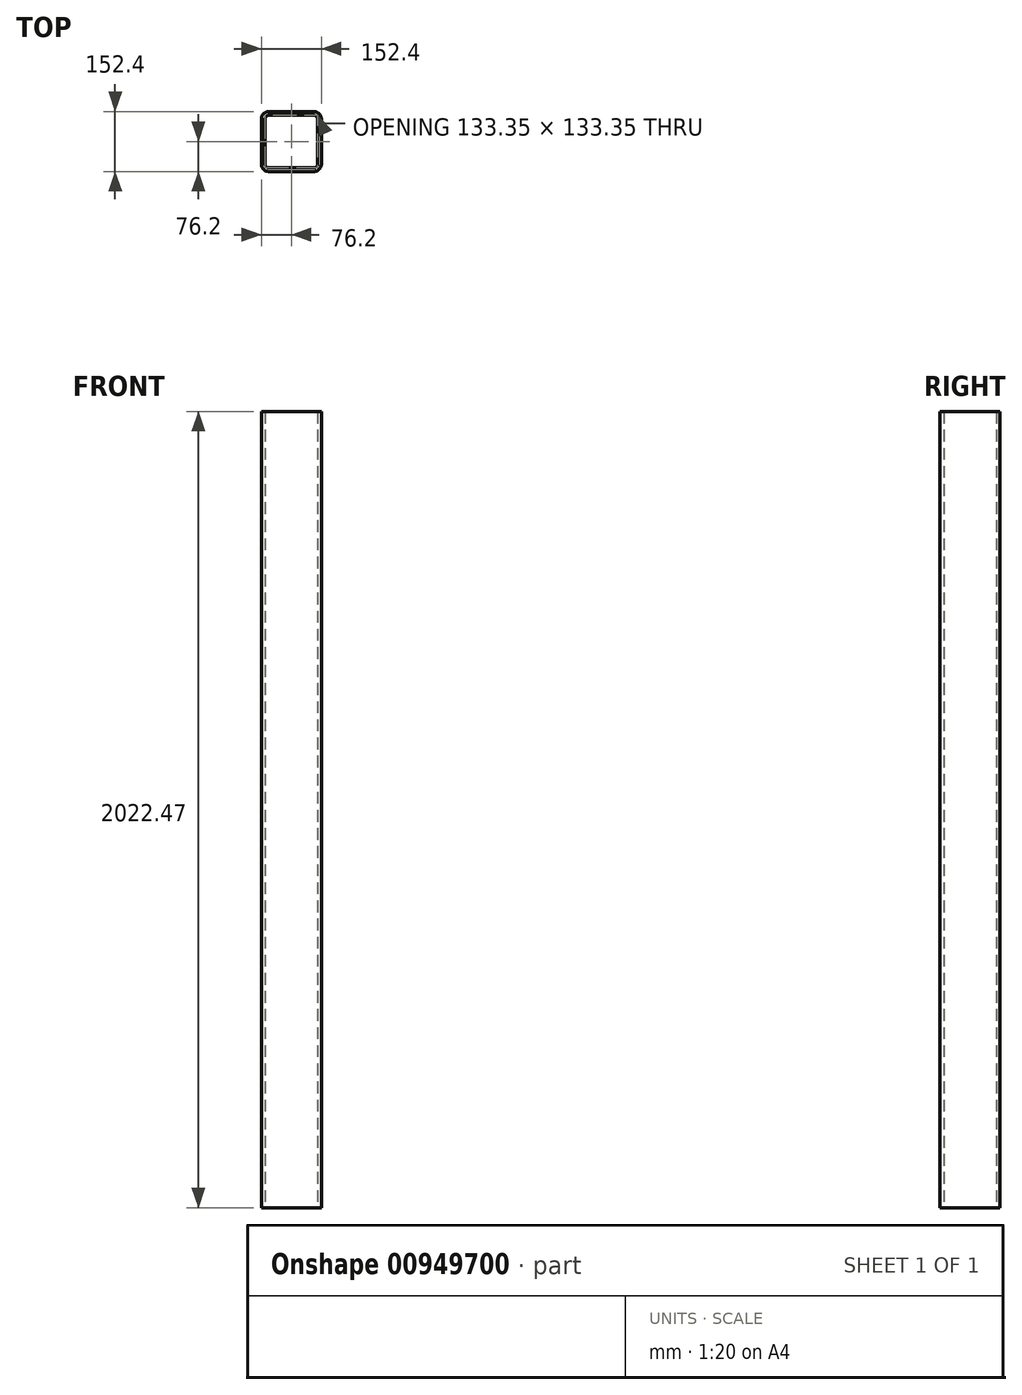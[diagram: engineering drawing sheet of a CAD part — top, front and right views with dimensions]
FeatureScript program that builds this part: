
annotation { "Feature Type Name" : "Feature", "Feature Type Description" : "" }
export const myFeature = defineFeature(function(context is Context, id is Id, definition is map)
    precondition{}
    {
        {
            var Q0;
            Q0=qCreatedBy(makeId("Top.planeOp"),FACE);
            var sketch = newSketch(context, id + "F0", { "sketchPlane" : qUnion([Q0])});
            skLineSegment(sketch, "E0.bottom", {"start": v(-57.15, -76.2) * mm, "end": v(57.15, -76.2) * mm});
            skLineSegment(sketch, "E0.top", {"start": v(-57.15, 76.2) * mm, "end": v(57.15, 76.2) * mm});
            skLineSegment(sketch, "E0.left", {"start": v(-76.2, -57.15) * mm, "end": v(-76.2, 57.15) * mm});
            skLineSegment(sketch, "E0.right", {"start": v(76.2, -57.15) * mm, "end": v(76.2, 57.15) * mm});
            skPoint(sketch, "E0.middle", {"position": v(0, 0) * mm});
            skLineSegment(sketch, "E1.bottom", {"start": v(-57.15, -66.68) * mm, "end": v(57.15, -66.68) * mm});
            skLineSegment(sketch, "E1.top", {"start": v(-57.15, 66.68) * mm, "end": v(57.15, 66.68) * mm});
            skLineSegment(sketch, "E1.left", {"start": v(-66.68, -57.15) * mm, "end": v(-66.68, 57.15) * mm});
            skLineSegment(sketch, "E1.right", {"start": v(66.68, -57.15) * mm, "end": v(66.68, 57.15) * mm});
            skPoint(sketch, "E2.visualSharp", {"position": v(-76.2, 76.2) * mm});
            skArc(sketch, "E2.filletArc", {"start": v(-57.15, 76.2) * mm, "mid": v(-70.62, 70.62) * mm, "end": v(-76.2, 57.15) * mm});
            skPoint(sketch, "E3.visualSharp", {"position": v(-76.2, -76.2) * mm});
            skArc(sketch, "E3.filletArc", {"start": v(-76.2, -57.15) * mm, "mid": v(-70.62, -70.62) * mm, "end": v(-57.15, -76.2) * mm});
            skPoint(sketch, "E4.visualSharp", {"position": v(76.2, -76.2) * mm});
            skArc(sketch, "E4.filletArc", {"start": v(57.15, -76.2) * mm, "mid": v(70.62, -70.62) * mm, "end": v(76.2, -57.15) * mm});
            skPoint(sketch, "E5.visualSharp", {"position": v(76.2, 76.2) * mm});
            skArc(sketch, "E5.filletArc", {"start": v(76.2, 57.15) * mm, "mid": v(70.62, 70.62) * mm, "end": v(57.15, 76.2) * mm});
            skPoint(sketch, "E6.visualSharp", {"position": v(-66.68, 66.68) * mm});
            skArc(sketch, "E6.filletArc", {"start": v(-57.15, 66.68) * mm, "mid": v(-63.89, 63.89) * mm, "end": v(-66.68, 57.15) * mm});
            skPoint(sketch, "E7.visualSharp", {"position": v(-66.68, -66.68) * mm});
            skArc(sketch, "E7.filletArc", {"start": v(-66.68, -57.15) * mm, "mid": v(-63.89, -63.89) * mm, "end": v(-57.15, -66.68) * mm});
            skPoint(sketch, "E8.visualSharp", {"position": v(66.68, -66.68) * mm});
            skArc(sketch, "E8.filletArc", {"start": v(57.15, -66.68) * mm, "mid": v(63.89, -63.89) * mm, "end": v(66.68, -57.15) * mm});
            skPoint(sketch, "E9.visualSharp", {"position": v(66.68, 66.68) * mm});
            skArc(sketch, "E9.filletArc", {"start": v(66.68, 57.15) * mm, "mid": v(63.89, 63.89) * mm, "end": v(57.15, 66.68) * mm});
            skSolve(sketch);
        }
        {
            var Q0;
            Q0=qSketchRegion(id+"F0",true);
            extrude(context, id + "F1", {"entities" : qUnion([Q0]), "depth" : 2022.47 * mm, "offsetDistance" : 25.4 * mm});
        }
    });
